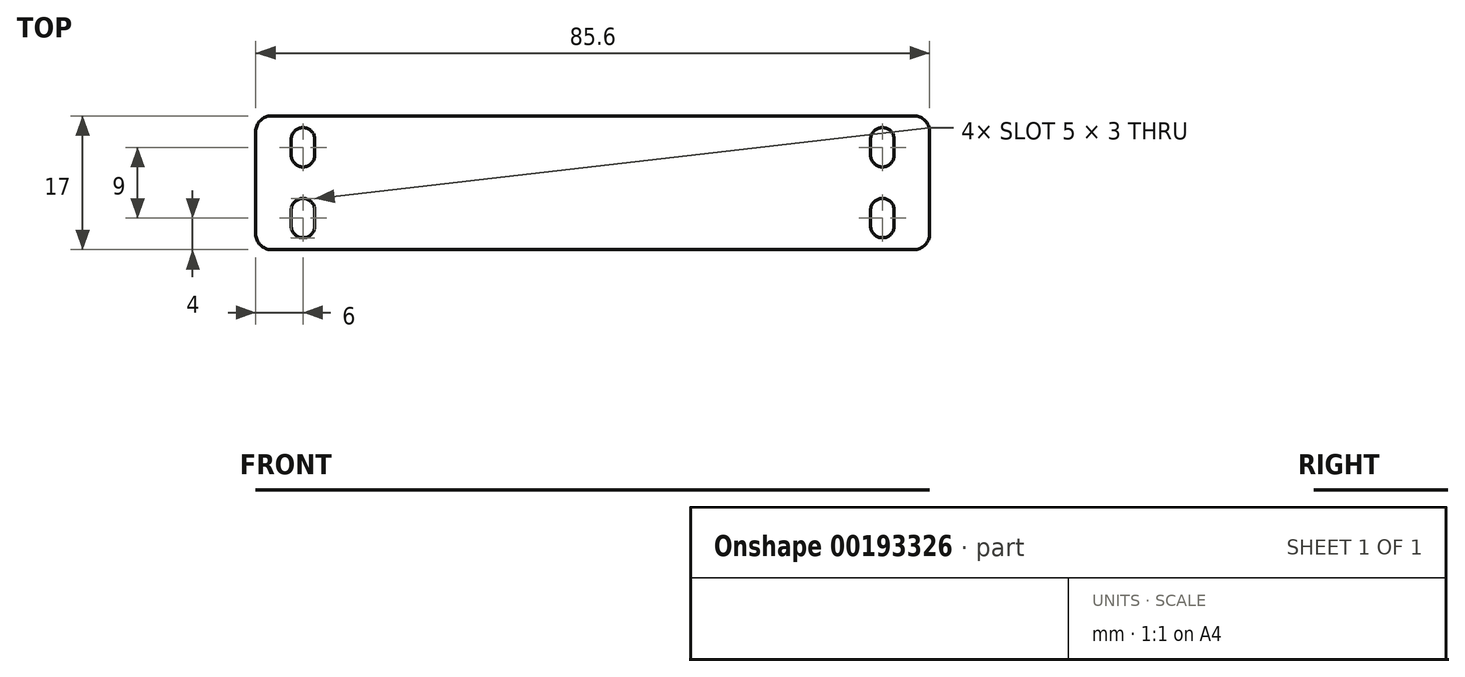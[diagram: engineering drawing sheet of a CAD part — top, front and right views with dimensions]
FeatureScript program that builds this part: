
annotation { "Feature Type Name" : "Feature", "Feature Type Description" : "" }
export const myFeature = defineFeature(function(context is Context, id is Id, definition is map)
    precondition{}
    {
        {
            var Q0;
            Q0=qCreatedBy(makeId("Top.planeOp"),FACE);
            var sketch = newSketch(context, id + "F0", { "sketchPlane" : qUnion([Q0])});
            skLineSegment(sketch, "E0.bottom", {"start": v(42.8, 8.5) * mm, "end": v(-42.8, 8.5) * mm});
            skLineSegment(sketch, "E0.top", {"start": v(42.8, -8.5) * mm, "end": v(-42.8, -8.5) * mm});
            skLineSegment(sketch, "E0.left", {"start": v(42.8, 8.5) * mm, "end": v(42.8, -8.5) * mm});
            skLineSegment(sketch, "E0.right", {"start": v(-42.8, 8.5) * mm, "end": v(-42.8, -8.5) * mm});
            skPoint(sketch, "E0.middle", {"position": v(0, 0) * mm});
            skArc(sketch, "E1", {"start": v(-35.3, 5.5) * mm, "mid": v(-36.8, 7) * mm, "end": v(-38.3, 5.5) * mm});
            skLineSegment(sketch, "E2", {"start": v(-36.8, 5.5) * mm, "end": v(-36.8, -5.5) * mm, "construction": true});
            skArc(sketch, "E3", {"start": v(-38.3, -5.5) * mm, "mid": v(-36.8, -7) * mm, "end": v(-35.3, -5.5) * mm});
            skArc(sketch, "E4", {"start": v(-35.3, -3.5) * mm, "mid": v(-36.8, -2) * mm, "end": v(-38.3, -3.5) * mm});
            skArc(sketch, "E5", {"start": v(-38.3, 3.5) * mm, "mid": v(-36.8, 2) * mm, "end": v(-35.3, 3.5) * mm});
            skLineSegment(sketch, "E6", {"start": v(-35.3, 3.5) * mm, "end": v(-35.3, 5.5) * mm});
            skLineSegment(sketch, "E7", {"start": v(-38.3, 5.5) * mm, "end": v(-38.3, 3.5) * mm});
            skLineSegment(sketch, "E8", {"start": v(-35.3, -3.5) * mm, "end": v(-35.3, -5.5) * mm});
            skLineSegment(sketch, "E9", {"start": v(-38.3, -3.5) * mm, "end": v(-38.3, -5.5) * mm});
            skPoint(sketch, "E10", {"position": v(-36.8, 0) * mm});
            skArc(sketch, "E11.MirrorCS", {"start": v(35.3, 5.5) * mm, "mid": v(36.8, 7) * mm, "end": v(38.3, 5.5) * mm});
            skLineSegment(sketch, "E12.MirrorCS", {"start": v(36.8, 5.5) * mm, "end": v(36.8, -5.5) * mm, "construction": true});
            skLineSegment(sketch, "E13.MirrorCS", {"start": v(38.3, -3.5) * mm, "end": v(38.3, -5.5) * mm});
            skLineSegment(sketch, "E14.MirrorCS", {"start": v(35.3, -3.5) * mm, "end": v(35.3, -5.5) * mm});
            skPoint(sketch, "E15.MirrorP", {"position": v(36.8, 0) * mm});
            skArc(sketch, "E16.MirrorCS", {"start": v(38.3, -5.5) * mm, "mid": v(36.8, -7) * mm, "end": v(35.3, -5.5) * mm});
            skLineSegment(sketch, "E17.MirrorCS", {"start": v(35.3, 3.5) * mm, "end": v(35.3, 5.5) * mm});
            skArc(sketch, "E18.MirrorCS", {"start": v(38.3, 3.5) * mm, "mid": v(36.8, 2) * mm, "end": v(35.3, 3.5) * mm});
            skArc(sketch, "E19.MirrorCS", {"start": v(35.3, -3.5) * mm, "mid": v(36.8, -2) * mm, "end": v(38.3, -3.5) * mm});
            skLineSegment(sketch, "E20.MirrorCS", {"start": v(38.3, 5.5) * mm, "end": v(38.3, 3.5) * mm});
            skSolve(sketch);
        }
        {
            var Q0;
            Q0=makeQuery(id+"F0.imprint","IMPRINT",FACE,{"disambiguationData":[TD([[makeQuery(id+"F0.imprint","IMPRINT",EDGE,{"derivedFrom":sQuery(id+"F0.wireOp",EDGE,"E0.bottom")}),1.0]])]});
            extrude(context, id + "F1", {"entities" : qUnion([Q0]), "depth" : 1 / 406.4 * mm});
        }
        {
            var Q0;
            Q0=makeQuery(id+"F1.opExtrude","SWEPT_EDGE",EDGE,{"disambiguationData":[OSD([sQuery(id+"F0.wireOp",EDGE,"E0.top"),sQuery(id+"F0.wireOp",EDGE,"E0.right")])]});
            var Q1;
            Q1=makeQuery(id+"F1.opExtrude","SWEPT_EDGE",EDGE,{"disambiguationData":[OSD([sQuery(id+"F0.wireOp",EDGE,"E0.bottom"),sQuery(id+"F0.wireOp",EDGE,"E0.right")])]});
            var Q2;
            Q2=makeQuery(id+"F1.opExtrude","SWEPT_EDGE",EDGE,{"disambiguationData":[OSD([sQuery(id+"F0.wireOp",EDGE,"E0.bottom"),sQuery(id+"F0.wireOp",EDGE,"E0.left")])]});
            var Q3;
            Q3=makeQuery(id+"F1.opExtrude","SWEPT_EDGE",EDGE,{"disambiguationData":[OSD([sQuery(id+"F0.wireOp",EDGE,"E0.top"),sQuery(id+"F0.wireOp",EDGE,"E0.left")])]});
            fillet(context, id + "F2", {"entities" : qUnion([Q0, Q1, Q2, Q3]), "radius" : 2 * mm, "tangentPropagation" : true, "allowEdgeOverflow" : false});
        }
    });
